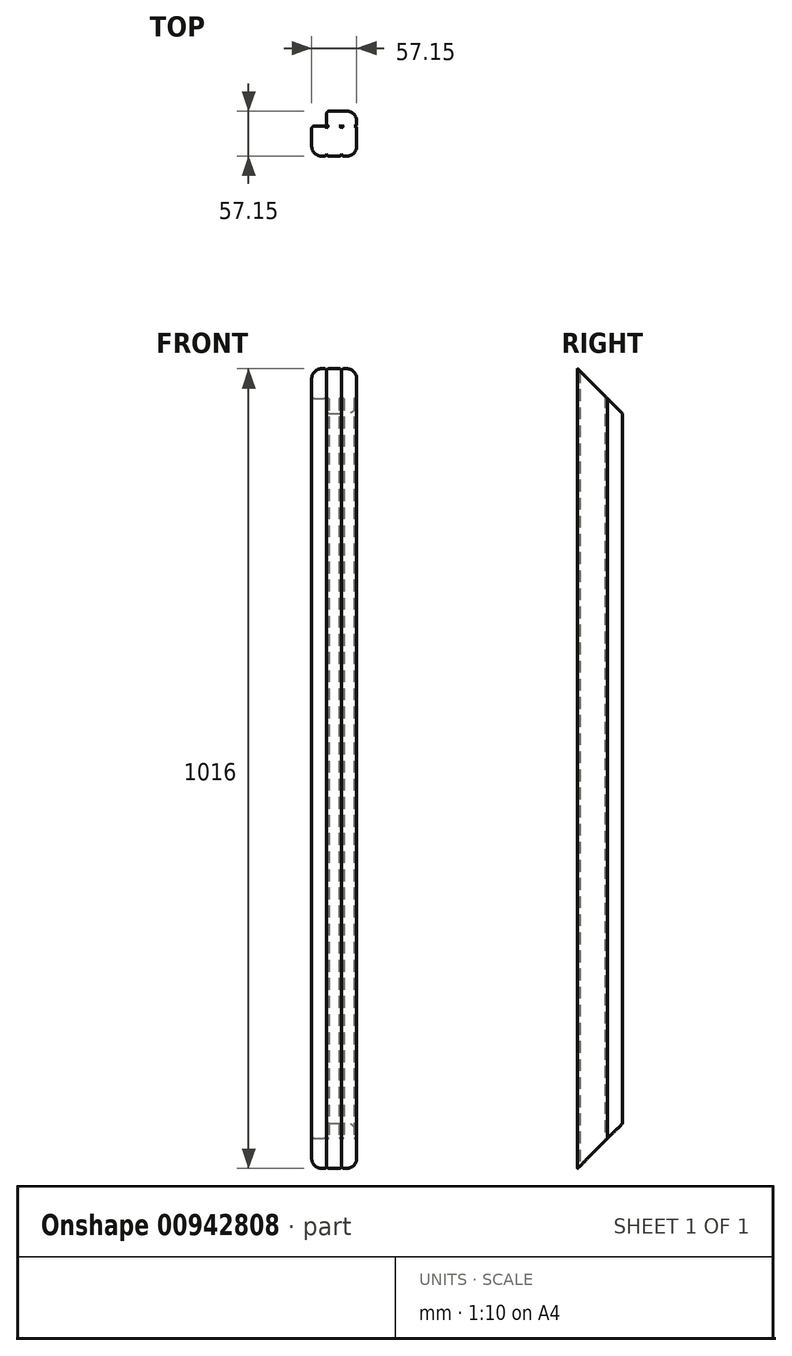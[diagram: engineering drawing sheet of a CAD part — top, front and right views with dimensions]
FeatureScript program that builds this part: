
annotation { "Feature Type Name" : "Feature", "Feature Type Description" : "" }
export const myFeature = defineFeature(function(context is Context, id is Id, definition is map)
    precondition{}
    {
        {
            var Q0;
            Q0=qCreatedBy(makeId("Top.planeOp"),FACE);
            var sketch = newSketch(context, id + "F0", { "sketchPlane" : qUnion([Q0])});
            skLineSegment(sketch, "E0.bottom", {"start": v(12.7, 0) * mm, "end": v(15.9, 0) * mm});
            skLineSegment(sketch, "E0.top", {"start": v(3.15, 38.1) * mm, "end": v(15.9, 38.1) * mm});
            skLineSegment(sketch, "E0.left", {"start": v(0, 12.7) * mm, "end": v(0, 34.95) * mm});
            skLineSegment(sketch, "E0.right", {"start": v(19.05, 3.15) * mm, "end": v(19.05, 34.95) * mm});
            skPoint(sketch, "E1.visualSharp", {"position": v(0, 38.1) * mm});
            skArc(sketch, "E1.filletArc", {"start": v(3.15, 38.1) * mm, "mid": v(0.92, 37.18) * mm, "end": v(0, 34.95) * mm});
            skPoint(sketch, "E2.visualSharp", {"position": v(19.05, 38.1) * mm});
            skArc(sketch, "E2.filletArc", {"start": v(19.05, 34.95) * mm, "mid": v(18.13, 37.18) * mm, "end": v(15.9, 38.1) * mm});
            skPoint(sketch, "E3.visualSharp", {"position": v(19.05, 0) * mm});
            skArc(sketch, "E3.filletArc", {"start": v(15.9, 0) * mm, "mid": v(18.13, 0.92) * mm, "end": v(19.05, 3.15) * mm});
            skPoint(sketch, "E4.visualSharp", {"position": v(0, 0) * mm});
            skArc(sketch, "E4.filletArc", {"start": v(0, 12.7) * mm, "mid": v(3.72, 3.72) * mm, "end": v(12.7, 0) * mm});
            skLineSegment(sketch, "E5.bottom", {"start": v(22.2, 0) * mm, "end": v(34.95, 0) * mm});
            skLineSegment(sketch, "E5.top", {"start": v(22.2, 38.1) * mm, "end": v(34.95, 38.1) * mm});
            skLineSegment(sketch, "E5.right", {"start": v(38.1, 3.15) * mm, "end": v(38.1, 34.95) * mm});
            skArc(sketch, "E6.filletArc", {"start": v(22.2, 38.1) * mm, "mid": v(19.97, 37.18) * mm, "end": v(19.05, 34.95) * mm});
            skPoint(sketch, "E7.visualSharp", {"position": v(38.1, 38.1) * mm});
            skArc(sketch, "E7.filletArc", {"start": v(38.1, 34.95) * mm, "mid": v(37.18, 37.18) * mm, "end": v(34.95, 38.1) * mm});
            skPoint(sketch, "E8.visualSharp", {"position": v(38.1, 0) * mm});
            skArc(sketch, "E8.filletArc", {"start": v(34.95, 0) * mm, "mid": v(37.18, 0.92) * mm, "end": v(38.1, 3.15) * mm});
            skArc(sketch, "E9.filletArc", {"start": v(19.05, 3.15) * mm, "mid": v(19.97, 0.92) * mm, "end": v(22.2, 0) * mm});
            skLineSegment(sketch, "E10.bottom", {"start": v(41.25, 0) * mm, "end": v(44.45, 0) * mm});
            skLineSegment(sketch, "E10.top", {"start": v(41.25, 38.1) * mm, "end": v(54, 38.1) * mm});
            skLineSegment(sketch, "E10.right", {"start": v(57.15, 12.7) * mm, "end": v(57.15, 34.95) * mm});
            skArc(sketch, "E11.filletArc", {"start": v(41.25, 38.1) * mm, "mid": v(39.02, 37.18) * mm, "end": v(38.1, 34.95) * mm});
            skPoint(sketch, "E12.visualSharp", {"position": v(57.15, 38.1) * mm});
            skArc(sketch, "E12.filletArc", {"start": v(57.15, 34.95) * mm, "mid": v(56.23, 37.18) * mm, "end": v(54, 38.1) * mm});
            skPoint(sketch, "E13.visualSharp", {"position": v(57.15, 0) * mm});
            skArc(sketch, "E13.filletArc", {"start": v(44.45, 0) * mm, "mid": v(53.43, 3.72) * mm, "end": v(57.15, 12.7) * mm});
            skArc(sketch, "E14.filletArc", {"start": v(38.1, 3.15) * mm, "mid": v(39.02, 0.92) * mm, "end": v(41.25, 0) * mm});
            skLineSegment(sketch, "E15.bottom", {"start": v(57.15, 41.25) * mm, "end": v(57.15, 44.45) * mm});
            skLineSegment(sketch, "E15.top", {"start": v(19.05, 41.25) * mm, "end": v(19.05, 54) * mm});
            skLineSegment(sketch, "E15.left", {"start": v(54, 38.1) * mm, "end": v(22.2, 38.1) * mm});
            skLineSegment(sketch, "E15.right", {"start": v(44.45, 57.15) * mm, "end": v(22.2, 57.15) * mm});
            skArc(sketch, "E16.filletArc", {"start": v(19.05, 41.25) * mm, "mid": v(19.97, 39.02) * mm, "end": v(22.2, 38.1) * mm});
            skPoint(sketch, "E17.visualSharp", {"position": v(19.05, 57.15) * mm});
            skArc(sketch, "E17.filletArc", {"start": v(22.2, 57.15) * mm, "mid": v(19.97, 56.23) * mm, "end": v(19.05, 54) * mm});
            skPoint(sketch, "E18.visualSharp", {"position": v(57.15, 57.15) * mm});
            skArc(sketch, "E18.filletArc", {"start": v(57.15, 44.45) * mm, "mid": v(53.43, 53.43) * mm, "end": v(44.45, 57.15) * mm});
            skArc(sketch, "E19.filletArc", {"start": v(54, 38.1) * mm, "mid": v(56.23, 39.02) * mm, "end": v(57.15, 41.25) * mm});
            skSolve(sketch);
        }
        {
            var Q0;
            Q0=makeQuery(id+"F0.imprint","IMPRINT",FACE,{"disambiguationData":[TD([[makeQuery(id+"F0.imprint","IMPRINT",EDGE,{"derivedFrom":sQuery(id+"F0.wireOp",EDGE,"E0.bottom")}),1.0]])]});
            var Q1;
            Q1=makeQuery(id+"F0.imprint","IMPRINT",FACE,{"disambiguationData":[TD([[makeQuery(id+"F0.imprint","IMPRINT",EDGE,{"derivedFrom":sQuery(id+"F0.wireOp",EDGE,"E5.bottom")}),1.0]])]});
            var Q2;
            Q2=makeQuery(id+"F0.imprint","IMPRINT",FACE,{"disambiguationData":[TD([[makeQuery(id+"F0.imprint","IMPRINT",EDGE,{"derivedFrom":sQuery(id+"F0.wireOp",EDGE,"E10.bottom")}),1.0]])]});
            var Q3;
            Q3=makeQuery(id+"F0.imprint","IMPRINT",FACE,{"disambiguationData":[TD([[makeQuery(id+"F0.imprint","IMPRINT",EDGE,{"derivedFrom":sQuery(id+"F0.wireOp",EDGE,"E15.bottom")}),1.0]])]});
            extrude(context, id + "F1", {"entities" : qUnion([Q0, Q1, Q2, Q3]), "depth" : 1016 * mm, "offsetDistance" : 25.4 * mm});
        }
        {
            var Q0;
            Q0=makeQuery(id+"F1.opExtrude","SWEPT_FACE",FACE,{"disambiguationData":[OSD([sQuery(id+"F0.wireOp",EDGE,"E10.right")])]});
            var sketch = newSketch(context, id + "F2", { "sketchPlane" : qUnion([Q0])});
            skLineSegment(sketch, "E20.0", {"start": v(0, 1016) * mm, "end": v(12.7, 1016) * mm});
            skLineSegment(sketch, "E21.0", {"start": v(57.15, 1016) * mm, "end": v(57.15, 0) * mm});
            skLineSegment(sketch, "E22.0", {"start": v(0, 0) * mm, "end": v(12.7, 0) * mm});
            skLineSegment(sketch, "E23", {"start": v(0, 1016) * mm, "end": v(57.15, 1016) * mm});
            skLineSegment(sketch, "E24", {"start": v(57.15, 1016) * mm, "end": v(57.15, 958.85) * mm});
            skLineSegment(sketch, "E25", {"start": v(57.15, 958.85) * mm, "end": v(0, 1016) * mm});
            skLineSegment(sketch, "E26", {"start": v(0, 0) * mm, "end": v(57.15, 0) * mm});
            skLineSegment(sketch, "E27", {"start": v(57.15, 0) * mm, "end": v(57.15, 57.15) * mm});
            skLineSegment(sketch, "E28", {"start": v(57.15, 57.15) * mm, "end": v(0, 0) * mm});
            skLineSegment(sketch, "E29", {"start": v(57.15, 57.15) * mm, "end": v(57.15, 0) * mm});
            skSolve(sketch);
        }
        {
            var Q0;
            Q0=qSketchRegion(id+"F2",true);
            extrude(context, id + "F3", {"entities" : qUnion([Q0]), "operationType" : NewBodyOperationType.REMOVE, "endBound" : BoundingType.THROUGH_ALL, "oppositeDirection" : true, "depth" : 25.4 * mm, "offsetDistance" : 25.4 * mm});
        }
    });
